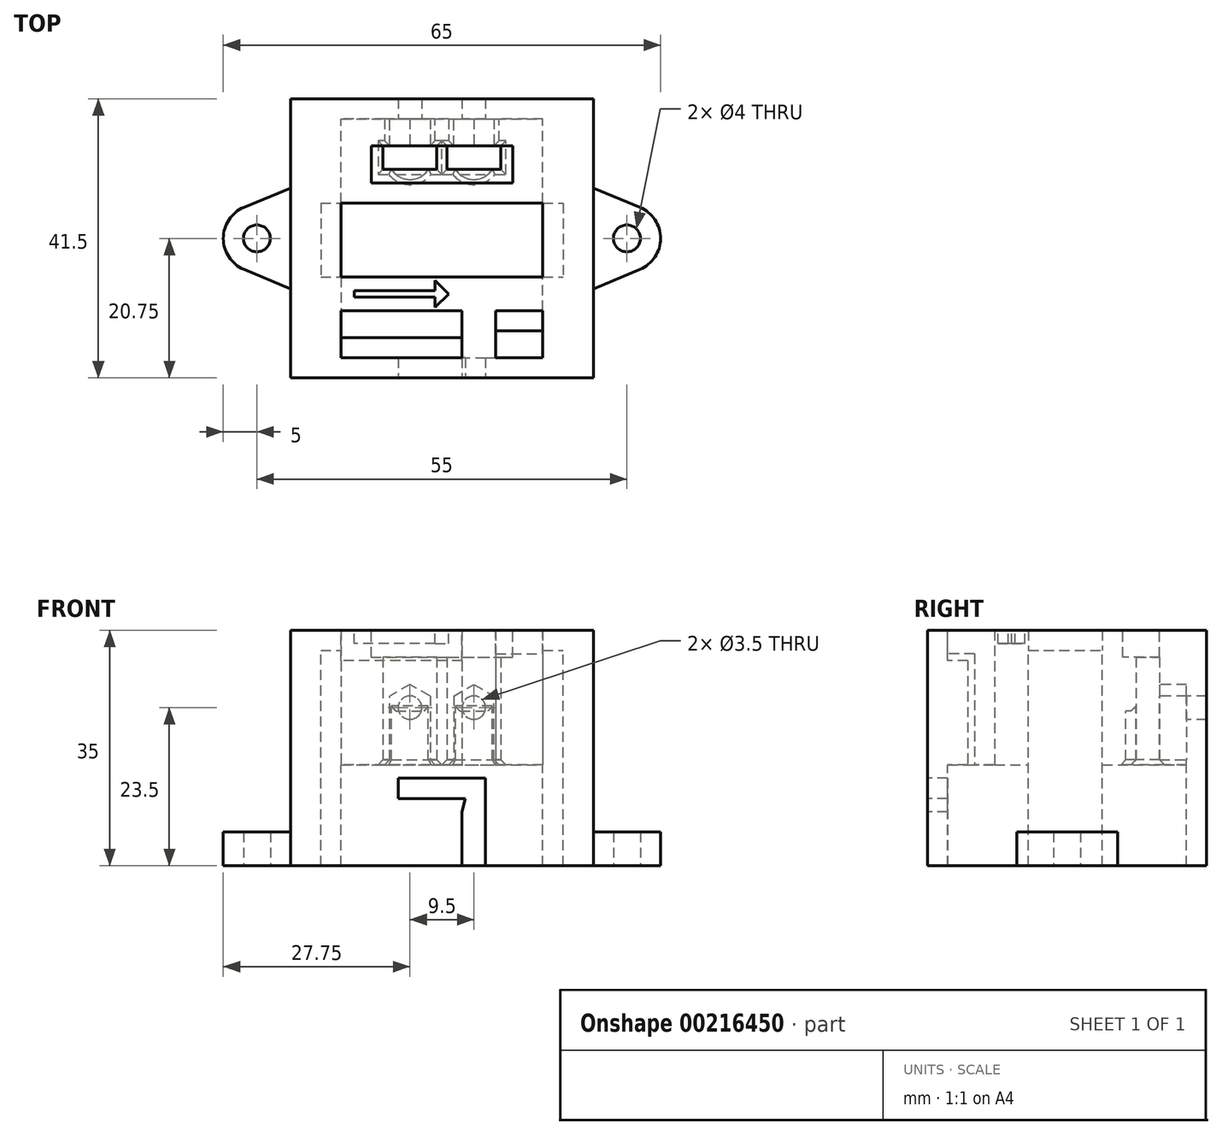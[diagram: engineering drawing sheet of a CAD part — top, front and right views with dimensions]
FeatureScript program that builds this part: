
annotation { "Feature Type Name" : "Feature", "Feature Type Description" : "" }
export const myFeature = defineFeature(function(context is Context, id is Id, definition is map)
    precondition{}
    {
        {
            var Q0;
            Q0=qCreatedBy(makeId("Top.planeOp"),FACE);
            var sketch = newSketch(context, id + "F0", { "sketchPlane" : qUnion([Q0])});
            skLineSegment(sketch, "E0.bottom", {"start": v(-22.5, 20.75) * mm, "end": v(22.5, 20.75) * mm});
            skLineSegment(sketch, "E0.top", {"start": v(-22.5, -20.75) * mm, "end": v(22.5, -20.75) * mm});
            skLineSegment(sketch, "E0.left", {"start": v(-22.5, 20.75) * mm, "end": v(-22.5, -20.75) * mm});
            skLineSegment(sketch, "E0.right", {"start": v(22.5, 20.75) * mm, "end": v(22.5, -20.75) * mm});
            skPoint(sketch, "E1", {"position": v(-22.5, 0) * mm});
            skPoint(sketch, "E2", {"position": v(0, 20.75) * mm});
            skLineSegment(sketch, "E3.bottom", {"start": v(-15, -5.75) * mm, "end": v(15, -5.75) * mm});
            skLineSegment(sketch, "E3.top", {"start": v(-15, 5.25) * mm, "end": v(15, 5.25) * mm});
            skLineSegment(sketch, "E3.left", {"start": v(-15, -5.75) * mm, "end": v(-15, 5.25) * mm});
            skLineSegment(sketch, "E3.right", {"start": v(15, -5.75) * mm, "end": v(15, 5.25) * mm});
            skPoint(sketch, "E4", {"position": v(0, 5.25) * mm});
            skLineSegment(sketch, "E5.bottom", {"start": v(-10.5, 13.75) * mm, "end": v(10.5, 13.75) * mm, "construction": true});
            skLineSegment(sketch, "E5.top", {"start": v(-10.5, 8.25) * mm, "end": v(10.5, 8.25) * mm, "construction": true});
            skLineSegment(sketch, "E5.left", {"start": v(-10.5, 13.75) * mm, "end": v(-10.5, 8.25) * mm, "construction": true});
            skLineSegment(sketch, "E5.right", {"start": v(10.5, 13.75) * mm, "end": v(10.5, 8.25) * mm, "construction": true});
            skPoint(sketch, "E6", {"position": v(0, 13.75) * mm});
            skLineSegment(sketch, "E7", {"start": v(0.75, 10.25) * mm, "end": v(0.75, 13.75) * mm});
            skLineSegment(sketch, "E8", {"start": v(0.75, 13.75) * mm, "end": v(8.75, 13.75) * mm});
            skLineSegment(sketch, "E9", {"start": v(8.75, 13.75) * mm, "end": v(8.75, 10.25) * mm});
            skLineSegment(sketch, "E10", {"start": v(0.75, 10.25) * mm, "end": v(8.75, 10.25) * mm});
            skLineSegment(sketch, "E11.MirrorCS", {"start": v(-0.75, 10.25) * mm, "end": v(-0.75, 13.75) * mm});
            skLineSegment(sketch, "E12.MirrorCS", {"start": v(-0.75, 13.75) * mm, "end": v(-8.75, 13.75) * mm});
            skLineSegment(sketch, "E13.MirrorCS", {"start": v(-8.75, 13.75) * mm, "end": v(-8.75, 10.25) * mm});
            skLineSegment(sketch, "E14", {"start": v(-0.75, 10.25) * mm, "end": v(-8.75, 10.25) * mm});
            skLineSegment(sketch, "E15", {"start": v(-15, -10.75) * mm, "end": v(3, -10.75) * mm});
            skLineSegment(sketch, "E16", {"start": v(-15, -10.75) * mm, "end": v(-15, -14.75) * mm});
            skLineSegment(sketch, "E17", {"start": v(3, -14.75) * mm, "end": v(-15, -14.75) * mm});
            skLineSegment(sketch, "E18", {"start": v(3, -14.75) * mm, "end": v(3, -10.75) * mm});
            skLineSegment(sketch, "E19", {"start": v(3, -14.75) * mm, "end": v(3, -17.75) * mm, "construction": true});
            skLineSegment(sketch, "E20", {"start": v(-15, -17.75) * mm, "end": v(3, -17.75) * mm, "construction": true});
            skLineSegment(sketch, "E21", {"start": v(-15, -17.75) * mm, "end": v(-15, -14.75) * mm, "construction": true});
            skLineSegment(sketch, "E22", {"start": v(8, -10.75) * mm, "end": v(8, -13.75) * mm});
            skLineSegment(sketch, "E23", {"start": v(8, -13.75) * mm, "end": v(15, -13.75) * mm});
            skLineSegment(sketch, "E24", {"start": v(15, -13.75) * mm, "end": v(15, -10.75) * mm});
            skLineSegment(sketch, "E25", {"start": v(15, -10.75) * mm, "end": v(8, -10.75) * mm});
            skLineSegment(sketch, "E26", {"start": v(8, -13.75) * mm, "end": v(8, -17.75) * mm, "construction": true});
            skLineSegment(sketch, "E27", {"start": v(8, -17.75) * mm, "end": v(15, -17.75) * mm, "construction": true});
            skLineSegment(sketch, "E28", {"start": v(15, -17.75) * mm, "end": v(15, -13.75) * mm, "construction": true});
            skLineSegment(sketch, "E29", {"start": v(-15, -20.75) * mm, "end": v(15, -20.75) * mm, "construction": true});
            skPoint(sketch, "E30", {"position": v(0, -20.75) * mm});
            skSolve(sketch);
        }
        {
            var Q0;
            Q0 = qSketchRegion(id + "F0", true);
            extrude(context, id + "F1", {"entities" : qUnion([Q0]), "depth" : 35 * mm});
        }
        {
            var Q0;
            Q0=makeQuery(id+"F1.opExtrude","CAP_FACE",FACE,{"disambiguationData":[OSD([sQuery(id+"F0.wireOp",EDGE,"E0.bottom"),sQuery(id+"F0.wireOp",EDGE,"E0.top"),sQuery(id+"F0.wireOp",EDGE,"E0.left"),sQuery(id+"F0.wireOp",EDGE,"E0.right"),sQuery(id+"F0.wireOp",EDGE,"E3.bottom"),sQuery(id+"F0.wireOp",EDGE,"E3.top"),sQuery(id+"F0.wireOp",EDGE,"E3.left"),sQuery(id+"F0.wireOp",EDGE,"E3.right"),sQuery(id+"F0.wireOp",EDGE,"E7"),sQuery(id+"F0.wireOp",EDGE,"E8"),sQuery(id+"F0.wireOp",EDGE,"E9"),sQuery(id+"F0.wireOp",EDGE,"E10"),sQuery(id+"F0.wireOp",EDGE,"E11.MirrorCS"),sQuery(id+"F0.wireOp",EDGE,"E12.MirrorCS"),sQuery(id+"F0.wireOp",EDGE,"E13.MirrorCS"),sQuery(id+"F0.wireOp",EDGE,"E14")])],"isStart":false});
            var sketch = newSketch(context, id + "F2", { "sketchPlane" : qUnion([Q0])});
            skLineSegment(sketch, "E31.bottom", {"start": v(-10.5, 13.75) * mm, "end": v(10.5, 13.75) * mm});
            skLineSegment(sketch, "E31.top", {"start": v(-10.5, 8.25) * mm, "end": v(10.5, 8.25) * mm});
            skLineSegment(sketch, "E31.left", {"start": v(-10.5, 13.75) * mm, "end": v(-10.5, 8.25) * mm});
            skLineSegment(sketch, "E31.right", {"start": v(10.5, 13.75) * mm, "end": v(10.5, 8.25) * mm});
            skSolve(sketch);
        }
        {
            var Q0;
            Q0 = qSketchRegion(id + "F2", true);
            extrude(context, id + "F3", {"entities" : qUnion([Q0]), "operationType" : NewBodyOperationType.REMOVE, "oppositeDirection" : true, "depth" : 4 * mm});
        }
        {
            var Q0;
            Q0=makeQuery(id+"F1.opExtrude","SWEPT_FACE",FACE,{"disambiguationData":[OSD([sQuery(id+"F0.wireOp",EDGE,"E8")])]});
            var sketch = newSketch(context, id + "F4", { "sketchPlane" : qUnion([Q0])});
            skCircle(sketch, "E32", {"center": v(4.75, 23.5) * mm, "radius": 1.75 * mm});
            skPoint(sketch, "E33", {"position": v(4.75, 31) * mm});
            skCircle(sketch, "E34.MirrorC", {"center": v(-4.75, 23.5) * mm, "radius": 1.75 * mm});
            skLineSegment(sketch, "E35", {"start": v(0.75, 31) * mm, "end": v(8.75, 31) * mm, "construction": true});
            skSolve(sketch);
        }
        {
            var Q0;
            Q0 = qSketchRegion(id + "F4", true);
            extrude(context, id + "F5", {"entities" : qUnion([Q0]), "operationType" : NewBodyOperationType.REMOVE, "oppositeDirection" : true, "depth" : 25 * mm});
        }
        {
            var Q0;
            Q0=makeQuery(id+"F1.opExtrude","SWEPT_FACE",FACE,{"disambiguationData":[OSD([sQuery(id+"F0.wireOp",EDGE,"E8")])]});
            var sketch = newSketch(context, id + "F6", { "sketchPlane" : qUnion([Q0])});
            skCircle(sketch, "E36.cCircle", {"center": v(4.75, 23.5) * mm, "radius": 3 * mm, "construction": true});
            skLineSegment(sketch, "E36.0", {"start": v(1.75, 25.23) * mm, "end": v(4.75, 26.96) * mm});
            skLineSegment(sketch, "E36.1", {"start": v(4.75, 26.96) * mm, "end": v(7.75, 25.23) * mm});
            skLineSegment(sketch, "E36.2", {"start": v(7.75, 25.23) * mm, "end": v(7.75, 21.77) * mm});
            skLineSegment(sketch, "E36.5", {"start": v(1.75, 21.77) * mm, "end": v(1.75, 25.23) * mm});
            skPoint(sketch, "E36.0.midPoint", {"position": v(3.25, 26.1) * mm});
            skLineSegment(sketch, "E37", {"start": v(1.75, 21.77) * mm, "end": v(1.75, -5.3) * mm});
            skLineSegment(sketch, "E38", {"start": v(1.75, -5.3) * mm, "end": v(7.75, -5.3) * mm});
            skLineSegment(sketch, "E39", {"start": v(7.75, -5.3) * mm, "end": v(7.75, 21.77) * mm});
            skLineSegment(sketch, "E40.MirrorCS", {"start": v(-1.75, 25.23) * mm, "end": v(-4.75, 26.96) * mm});
            skLineSegment(sketch, "E41.MirrorCS", {"start": v(-4.75, 26.96) * mm, "end": v(-7.75, 25.23) * mm});
            skLineSegment(sketch, "E42.MirrorCS", {"start": v(-7.75, 25.23) * mm, "end": v(-7.75, 21.77) * mm});
            skLineSegment(sketch, "E43.MirrorCS", {"start": v(-7.75, -5.3) * mm, "end": v(-7.75, 21.77) * mm});
            skLineSegment(sketch, "E44.MirrorCS", {"start": v(-1.75, -5.3) * mm, "end": v(-7.75, -5.3) * mm});
            skLineSegment(sketch, "E45.MirrorCS", {"start": v(-1.75, 21.77) * mm, "end": v(-1.75, -5.3) * mm});
            skLineSegment(sketch, "E46.MirrorCS", {"start": v(-1.75, 21.77) * mm, "end": v(-1.75, 25.23) * mm});
            skSolve(sketch);
        }
        {
            var Q0;
            Q0 = qSketchRegion(id + "F6", true);
            extrude(context, id + "F7", {"entities" : qUnion([Q0]), "operationType" : NewBodyOperationType.REMOVE, "oppositeDirection" : true, "depth" : 4 * mm});
        }
        {
            var Q0;
            Q0=makeQuery(id+"F3.boolean.opBoolean","COPY",FACE,{"derivedFrom":makeQuery(id+"F3.opExtrude","CAP_FACE",FACE,{"disambiguationData":[OSD([sQuery(id+"F2.wireOp",EDGE,"E31.bottom"),sQuery(id+"F2.wireOp",EDGE,"E31.top"),sQuery(id+"F2.wireOp",EDGE,"E31.left"),sQuery(id+"F2.wireOp",EDGE,"E31.right")])],"isStart":false})});
            var sketch = newSketch(context, id + "F8", { "sketchPlane" : qUnion([Q0])});
            skPoint(sketch, "E47", {"position": v(4.75, 12) * mm});
            skPoint(sketch, "E48", {"position": v(8.75, 12) * mm});
            skCircle(sketch, "E49", {"center": v(4.75, 12) * mm, "radius": 3.25 * mm});
            skCircle(sketch, "E50.MirrorC", {"center": v(-4.75, 12) * mm, "radius": 3.25 * mm});
            skLineSegment(sketch, "E51", {"start": v(-8.75, 12) * mm, "end": v(-0.75, 12) * mm, "construction": true});
            skSolve(sketch);
        }
        {
            var Q0;
            Q0 = qSketchRegion(id + "F8", true);
            extrude(context, id + "F9", {"entities" : qUnion([Q0]), "operationType" : NewBodyOperationType.REMOVE, "oppositeDirection" : true, "depth" : 25 * mm, "hasSecondDirection" : true, "secondDirectionOppositeDirection" : true, "secondDirectionDepth" : 8 * mm});
        }
        {
            var Q0;
            Q0=makeQuery(id+"F1.opExtrude","CAP_FACE",FACE,{"disambiguationData":[OSD([sQuery(id+"F0.wireOp",EDGE,"E0.bottom"),sQuery(id+"F0.wireOp",EDGE,"E0.top"),sQuery(id+"F0.wireOp",EDGE,"E0.left"),sQuery(id+"F0.wireOp",EDGE,"E0.right"),sQuery(id+"F0.wireOp",EDGE,"E3.bottom"),sQuery(id+"F0.wireOp",EDGE,"E3.top"),sQuery(id+"F0.wireOp",EDGE,"E3.left"),sQuery(id+"F0.wireOp",EDGE,"E3.right"),sQuery(id+"F0.wireOp",EDGE,"E7"),sQuery(id+"F0.wireOp",EDGE,"E8"),sQuery(id+"F0.wireOp",EDGE,"E9"),sQuery(id+"F0.wireOp",EDGE,"E10"),sQuery(id+"F0.wireOp",EDGE,"E11.MirrorCS"),sQuery(id+"F0.wireOp",EDGE,"E12.MirrorCS"),sQuery(id+"F0.wireOp",EDGE,"E13.MirrorCS"),sQuery(id+"F0.wireOp",EDGE,"E14")])],"isStart":false});
            var sketch = newSketch(context, id + "F10", { "sketchPlane" : qUnion([Q0])});
            skLineSegment(sketch, "E52.bottom", {"start": v(-18, 5.25) * mm, "end": v(18, 5.25) * mm});
            skLineSegment(sketch, "E52.top", {"start": v(-18, -5.75) * mm, "end": v(18, -5.75) * mm});
            skLineSegment(sketch, "E52.left", {"start": v(-18, 5.25) * mm, "end": v(-18, -5.75) * mm});
            skLineSegment(sketch, "E52.right", {"start": v(18, 5.25) * mm, "end": v(18, -5.75) * mm});
            skPoint(sketch, "E53", {"position": v(0, 5.25) * mm});
            skSolve(sketch);
        }
        {
            var Q0;
            Q0 = qSketchRegion(id + "F10", true);
            extrude(context, id + "F11", {"entities" : qUnion([Q0]), "operationType" : NewBodyOperationType.REMOVE, "endBound" : BoundingType.THROUGH_ALL, "oppositeDirection" : true, "depth" : 25 * mm, "hasSecondDirection" : true, "secondDirectionOppositeDirection" : true, "secondDirectionDepth" : 3 * mm});
        }
        {
            var Q0;
            Q0=makeQuery(id+"F1.opExtrude","CAP_FACE",FACE,{"disambiguationData":[OSD([sQuery(id+"F0.wireOp",EDGE,"E0.bottom"),sQuery(id+"F0.wireOp",EDGE,"E0.top"),sQuery(id+"F0.wireOp",EDGE,"E0.left"),sQuery(id+"F0.wireOp",EDGE,"E0.right"),sQuery(id+"F0.wireOp",EDGE,"E3.bottom"),sQuery(id+"F0.wireOp",EDGE,"E3.top"),sQuery(id+"F0.wireOp",EDGE,"E3.left"),sQuery(id+"F0.wireOp",EDGE,"E3.right"),sQuery(id+"F0.wireOp",EDGE,"E7"),sQuery(id+"F0.wireOp",EDGE,"E8"),sQuery(id+"F0.wireOp",EDGE,"E9"),sQuery(id+"F0.wireOp",EDGE,"E10"),sQuery(id+"F0.wireOp",EDGE,"E11.MirrorCS"),sQuery(id+"F0.wireOp",EDGE,"E12.MirrorCS"),sQuery(id+"F0.wireOp",EDGE,"E13.MirrorCS"),sQuery(id+"F0.wireOp",EDGE,"E14"),sQuery(id+"F0.wireOp",EDGE,"E15"),sQuery(id+"F0.wireOp",EDGE,"E16"),sQuery(id+"F0.wireOp",EDGE,"E17"),sQuery(id+"F0.wireOp",EDGE,"E18")])],"isStart":false});
            var sketch = newSketch(context, id + "F12", { "sketchPlane" : qUnion([Q0])});
            skLineSegment(sketch, "E54.bottom", {"start": v(-15, -10.75) * mm, "end": v(3, -10.75) * mm});
            skLineSegment(sketch, "E54.top", {"start": v(-15, -17.75) * mm, "end": v(3, -17.75) * mm});
            skLineSegment(sketch, "E54.left", {"start": v(-15, -10.75) * mm, "end": v(-15, -17.75) * mm});
            skLineSegment(sketch, "E54.right", {"start": v(3, -10.75) * mm, "end": v(3, -17.75) * mm});
            skSolve(sketch);
        }
        {
            var Q0;
            Q0 = qSketchRegion(id + "F12", true);
            extrude(context, id + "F13", {"entities" : qUnion([Q0]), "operationType" : NewBodyOperationType.REMOVE, "oppositeDirection" : true, "depth" : 4.5 * mm});
        }
        {
            var Q0;
            Q0=makeQuery(id+"F1.opExtrude","CAP_FACE",FACE,{"disambiguationData":[OSD([sQuery(id+"F0.wireOp",EDGE,"E0.bottom"),sQuery(id+"F0.wireOp",EDGE,"E0.top"),sQuery(id+"F0.wireOp",EDGE,"E0.left"),sQuery(id+"F0.wireOp",EDGE,"E0.right"),sQuery(id+"F0.wireOp",EDGE,"E3.bottom"),sQuery(id+"F0.wireOp",EDGE,"E3.top"),sQuery(id+"F0.wireOp",EDGE,"E3.left"),sQuery(id+"F0.wireOp",EDGE,"E3.right"),sQuery(id+"F0.wireOp",EDGE,"E7"),sQuery(id+"F0.wireOp",EDGE,"E8"),sQuery(id+"F0.wireOp",EDGE,"E9"),sQuery(id+"F0.wireOp",EDGE,"E10"),sQuery(id+"F0.wireOp",EDGE,"E11.MirrorCS"),sQuery(id+"F0.wireOp",EDGE,"E12.MirrorCS"),sQuery(id+"F0.wireOp",EDGE,"E13.MirrorCS"),sQuery(id+"F0.wireOp",EDGE,"E14"),sQuery(id+"F0.wireOp",EDGE,"E15"),sQuery(id+"F0.wireOp",EDGE,"E16"),sQuery(id+"F0.wireOp",EDGE,"E17"),sQuery(id+"F0.wireOp",EDGE,"E18"),sQuery(id+"F0.wireOp",EDGE,"E22"),sQuery(id+"F0.wireOp",EDGE,"E23"),sQuery(id+"F0.wireOp",EDGE,"E24"),sQuery(id+"F0.wireOp",EDGE,"E25")])],"isStart":false});
            var sketch = newSketch(context, id + "F14", { "sketchPlane" : qUnion([Q0])});
            skLineSegment(sketch, "E55.bottom", {"start": v(8, -13.75) * mm, "end": v(15, -13.75) * mm});
            skLineSegment(sketch, "E55.top", {"start": v(8, -17.75) * mm, "end": v(15, -17.75) * mm});
            skLineSegment(sketch, "E55.left", {"start": v(8, -13.75) * mm, "end": v(8, -17.75) * mm});
            skLineSegment(sketch, "E55.right", {"start": v(15, -13.75) * mm, "end": v(15, -17.75) * mm});
            skSolve(sketch);
        }
        {
            var Q0;
            Q0 = qSketchRegion(id + "F14", true);
            extrude(context, id + "F15", {"entities" : qUnion([Q0]), "operationType" : NewBodyOperationType.REMOVE, "oppositeDirection" : true, "depth" : 3.5 * mm});
        }
        {
            var Q0;
            Q0=makeQuery(id+"F1.opExtrude","CAP_FACE",FACE,{"disambiguationData":[OSD([sQuery(id+"F0.wireOp",EDGE,"E0.bottom"),sQuery(id+"F0.wireOp",EDGE,"E0.top"),sQuery(id+"F0.wireOp",EDGE,"E0.left"),sQuery(id+"F0.wireOp",EDGE,"E0.right"),sQuery(id+"F0.wireOp",EDGE,"E3.bottom"),sQuery(id+"F0.wireOp",EDGE,"E3.top"),sQuery(id+"F0.wireOp",EDGE,"E3.left"),sQuery(id+"F0.wireOp",EDGE,"E3.right"),sQuery(id+"F0.wireOp",EDGE,"E7"),sQuery(id+"F0.wireOp",EDGE,"E8"),sQuery(id+"F0.wireOp",EDGE,"E9"),sQuery(id+"F0.wireOp",EDGE,"E10"),sQuery(id+"F0.wireOp",EDGE,"E11.MirrorCS"),sQuery(id+"F0.wireOp",EDGE,"E12.MirrorCS"),sQuery(id+"F0.wireOp",EDGE,"E13.MirrorCS"),sQuery(id+"F0.wireOp",EDGE,"E14")])],"isStart":false});
            var sketch = newSketch(context, id + "F16", { "sketchPlane" : qUnion([Q0])});
            skLineSegment(sketch, "E56.bottom", {"start": v(15, 5.25) * mm, "end": v(-15, 5.25) * mm});
            skLineSegment(sketch, "E56.top", {"start": v(15, 17.75) * mm, "end": v(-15, 17.75) * mm});
            skLineSegment(sketch, "E56.left", {"start": v(15, 5.25) * mm, "end": v(15, 17.75) * mm});
            skLineSegment(sketch, "E56.right", {"start": v(-15, 5.25) * mm, "end": v(-15, 17.75) * mm});
            skLineSegment(sketch, "E57.top", {"start": v(-15, -5.75) * mm, "end": v(15, -5.75) * mm});
            skLineSegment(sketch, "E57.left", {"start": v(-15, -17.75) * mm, "end": v(-15, -5.75) * mm});
            skLineSegment(sketch, "E57.right", {"start": v(15, -17.75) * mm, "end": v(15, -5.75) * mm});
            skLineSegment(sketch, "E58", {"start": v(-15, -17.75) * mm, "end": v(15, -17.75) * mm});
            skSolve(sketch);
        }
        {
            var Q0;
            Q0 = qSketchRegion(id + "F16", true);
            extrude(context, id + "F17", {"entities" : qUnion([Q0]), "operationType" : NewBodyOperationType.REMOVE, "endBound" : BoundingType.THROUGH_ALL, "oppositeDirection" : true, "depth" : 25 * mm, "hasSecondDirection" : true, "secondDirectionOppositeDirection" : true, "secondDirectionDepth" : 20 * mm});
        }
        {
            var Q0;
            Q0=makeQuery(id+"F1.opExtrude","CAP_FACE",FACE,{"disambiguationData":[OSD([sQuery(id+"F0.wireOp",EDGE,"E0.bottom"),sQuery(id+"F0.wireOp",EDGE,"E0.top"),sQuery(id+"F0.wireOp",EDGE,"E0.left"),sQuery(id+"F0.wireOp",EDGE,"E0.right"),sQuery(id+"F0.wireOp",EDGE,"E3.bottom"),sQuery(id+"F0.wireOp",EDGE,"E3.top"),sQuery(id+"F0.wireOp",EDGE,"E3.left"),sQuery(id+"F0.wireOp",EDGE,"E3.right"),sQuery(id+"F0.wireOp",EDGE,"E7"),sQuery(id+"F0.wireOp",EDGE,"E8"),sQuery(id+"F0.wireOp",EDGE,"E9"),sQuery(id+"F0.wireOp",EDGE,"E10"),sQuery(id+"F0.wireOp",EDGE,"E11.MirrorCS"),sQuery(id+"F0.wireOp",EDGE,"E12.MirrorCS"),sQuery(id+"F0.wireOp",EDGE,"E13.MirrorCS"),sQuery(id+"F0.wireOp",EDGE,"E14"),sQuery(id+"F0.wireOp",EDGE,"E15"),sQuery(id+"F0.wireOp",EDGE,"E16"),sQuery(id+"F0.wireOp",EDGE,"E17"),sQuery(id+"F0.wireOp",EDGE,"E18")])],"isStart":false});
            var sketch = newSketch(context, id + "F18", { "sketchPlane" : qUnion([Q0])});
            skLineSegment(sketch, "E59", {"start": v(-13, -7.75) * mm, "end": v(-13, -8.75) * mm});
            skLineSegment(sketch, "E60", {"start": v(-13, -8.75) * mm, "end": v(-1, -8.75) * mm});
            skLineSegment(sketch, "E61", {"start": v(-1, -8.75) * mm, "end": v(-1, -10.25) * mm});
            skLineSegment(sketch, "E62", {"start": v(-1, -10.25) * mm, "end": v(1, -8.25) * mm});
            skLineSegment(sketch, "E63", {"start": v(1, -8.25) * mm, "end": v(-1, -6.25) * mm});
            skLineSegment(sketch, "E64", {"start": v(-1, -6.25) * mm, "end": v(-1, -7.75) * mm});
            skLineSegment(sketch, "E65", {"start": v(-1, -7.75) * mm, "end": v(-13, -7.75) * mm});
            skPoint(sketch, "E66", {"position": v(-13, -8.25) * mm});
            skLineSegment(sketch, "E67", {"start": v(-13, -8.25) * mm, "end": v(1, -8.25) * mm, "construction": true});
            skPoint(sketch, "E68", {"position": v(-6, -8.25) * mm});
            skPoint(sketch, "E69", {"position": v(-6, -10.75) * mm});
            skLineSegment(sketch, "E70", {"start": v(-13, -5.75) * mm, "end": v(-13, -10.75) * mm, "construction": true});
            skSolve(sketch);
        }
        {
            var Q0;
            Q0 = qSketchRegion(id + "F18", true);
            extrude(context, id + "F19", {"entities" : qUnion([Q0]), "operationType" : NewBodyOperationType.REMOVE, "oppositeDirection" : true, "depth" : 2 * mm});
        }
        {
            var Q0;
            Q0=qCreatedBy(makeId("Top.planeOp"),FACE);
            var sketch = newSketch(context, id + "F20", { "sketchPlane" : qUnion([Q0])});
            skCircle(sketch, "E71", {"center": v(-27.5, 0) * mm, "radius": 2 * mm});
            skCircle(sketch, "E72.MirrorC", {"center": v(27.5, 0) * mm, "radius": 2 * mm});
            skArc(sketch, "E73", {"start": v(29.42, -4.62) * mm, "mid": v(32.5, 0) * mm, "end": v(29.42, 4.62) * mm});
            skLineSegment(sketch, "E74", {"start": v(22.5, -7.5) * mm, "end": v(22.5, 7.5) * mm});
            skLineSegment(sketch, "E75", {"start": v(22.5, 7.5) * mm, "end": v(29.42, 4.62) * mm});
            skLineSegment(sketch, "E76.MirrorCS", {"start": v(-22.5, -7.5) * mm, "end": v(-22.5, 7.5) * mm});
            skLineSegment(sketch, "E77.MirrorCS", {"start": v(-29.42, -4.62) * mm, "end": v(-22.5, -7.5) * mm});
            skArc(sketch, "E78.MirrorCS", {"start": v(-29.42, -4.62) * mm, "mid": v(-32.5, 0) * mm, "end": v(-29.42, 4.62) * mm});
            skLineSegment(sketch, "E79.MirrorCS", {"start": v(-22.5, 7.5) * mm, "end": v(-29.42, 4.62) * mm});
            skLineSegment(sketch, "E80.MirrorCS", {"start": v(22.5, -7.5) * mm, "end": v(29.42, -4.62) * mm});
            skSolve(sketch);
        }
        {
            var Q0;
            Q0 = qSketchRegion(id + "F20", true);
            extrude(context, id + "F21", {"entities" : qUnion([Q0]), "operationType" : NewBodyOperationType.ADD, "depth" : 5 * mm});
        }
        {
            var Q0;
            Q0=makeQuery(id+"F1.opExtrude","SWEPT_FACE",FACE,{"disambiguationData":[OSD([sQuery(id+"F0.wireOp",EDGE,"E0.top")])]});
            var sketch = newSketch(context, id + "F22", { "sketchPlane" : qUnion([Q0])});
            skLineSegment(sketch, "E81", {"start": v(3, 0) * mm, "end": v(3, 8) * mm});
            skLineSegment(sketch, "E82", {"start": v(6.5, 13) * mm, "end": v(6.5, 0) * mm});
            skLineSegment(sketch, "E83", {"start": v(3, 8) * mm, "end": v(3.5, 10) * mm});
            skLineSegment(sketch, "E84", {"start": v(3.5, 10) * mm, "end": v(-6.5, 10) * mm});
            skLineSegment(sketch, "E85", {"start": v(-6.5, 10) * mm, "end": v(-6.5, 13) * mm});
            skLineSegment(sketch, "E86", {"start": v(-6.5, 13) * mm, "end": v(6.5, 13) * mm});
            skPoint(sketch, "E87", {"position": v(0, 13) * mm});
            skLineSegment(sketch, "E88", {"start": v(3, 0) * mm, "end": v(6.5, 0) * mm});
            skSolve(sketch);
        }
        {
            var Q0;
            Q0 = qSketchRegion(id + "F22", true);
            extrude(context, id + "F23", {"entities" : qUnion([Q0]), "operationType" : NewBodyOperationType.REMOVE, "oppositeDirection" : true, "depth" : 10 * mm});
        }
        {
            var Q0;
            Q0=makeQuery(id+"F17.boolean.opBoolean","INTERSECT",EDGE,{"derivedFrom":[makeQuery(id+"F7.boolean.opBoolean","COPY",FACE,{"derivedFrom":makeQuery(id+"F7.opExtrude","SWEPT_FACE",FACE,{"disambiguationData":[OSD([sQuery(id+"F6.wireOp",EDGE,"E42.MirrorCS"),sQuery(id+"F6.wireOp",EDGE,"E43.MirrorCS")])]})}),makeQuery(id+"F17.opExtrude","CAP_FACE",FACE,{"disambiguationData":[OSD([sQuery(id+"F16.wireOp",EDGE,"E56.bottom"),sQuery(id+"F16.wireOp",EDGE,"E56.top"),sQuery(id+"F16.wireOp",EDGE,"E56.left"),sQuery(id+"F16.wireOp",EDGE,"E56.right")])],"isStart":true})]});
            var Q1;
            Q1=makeQuery(id+"F17.boolean.opBoolean","INTERSECT",EDGE,{"derivedFrom":[makeQuery(id+"F9.boolean.opBoolean","COPY",FACE,{"derivedFrom":makeQuery(id+"F9.opExtrude","SWEPT_FACE",FACE,{"disambiguationData":[OSD([sQuery(id+"F8.wireOp",EDGE,"E50.MirrorC")])]})}),makeQuery(id+"F17.opExtrude","CAP_FACE",FACE,{"disambiguationData":[OSD([sQuery(id+"F16.wireOp",EDGE,"E56.bottom"),sQuery(id+"F16.wireOp",EDGE,"E56.top"),sQuery(id+"F16.wireOp",EDGE,"E56.left"),sQuery(id+"F16.wireOp",EDGE,"E56.right")])],"isStart":true})]});
            var Q2;
            Q2=makeQuery(id+"F17.boolean.opBoolean","INTERSECT",EDGE,{"disambiguationData":[OD(3.0)],"derivedFrom":[makeQuery(id+"F3.boolean.opBoolean","MERGE",FACE,{"derivedFrom":[makeQuery(id+"F1.opExtrude","SWEPT_FACE",FACE,{"disambiguationData":[OSD([sQuery(id+"F0.wireOp",EDGE,"E10")])]}),makeQuery(id+"F1.opExtrude","SWEPT_FACE",FACE,{"disambiguationData":[OSD([sQuery(id+"F0.wireOp",EDGE,"E14")])]}),makeQuery(id+"F3.opExtrude","SWEPT_FACE",FACE,{"disambiguationData":[OSD([sQuery(id+"F2.wireOp",EDGE,"E31.top")])]})]}),makeQuery(id+"F17.opExtrude","CAP_FACE",FACE,{"disambiguationData":[OSD([sQuery(id+"F16.wireOp",EDGE,"E56.bottom"),sQuery(id+"F16.wireOp",EDGE,"E56.top"),sQuery(id+"F16.wireOp",EDGE,"E56.left"),sQuery(id+"F16.wireOp",EDGE,"E56.right")])],"isStart":true})]});
            var Q3;
            Q3=makeQuery(id+"F17.boolean.opBoolean","INTERSECT",EDGE,{"derivedFrom":[makeQuery(id+"F1.opExtrude","SWEPT_FACE",FACE,{"disambiguationData":[OSD([sQuery(id+"F0.wireOp",EDGE,"E13.MirrorCS")])]}),makeQuery(id+"F17.opExtrude","CAP_FACE",FACE,{"disambiguationData":[OSD([sQuery(id+"F16.wireOp",EDGE,"E56.bottom"),sQuery(id+"F16.wireOp",EDGE,"E56.top"),sQuery(id+"F16.wireOp",EDGE,"E56.left"),sQuery(id+"F16.wireOp",EDGE,"E56.right")])],"isStart":true})]});
            var Q4;
            Q4=makeQuery(id+"F17.boolean.opBoolean","INTERSECT",EDGE,{"disambiguationData":[OD(1.0)],"derivedFrom":[makeQuery(id+"F1.opExtrude","SWEPT_FACE",FACE,{"disambiguationData":[OSD([sQuery(id+"F0.wireOp",EDGE,"E12.MirrorCS")])]}),makeQuery(id+"F17.opExtrude","CAP_FACE",FACE,{"disambiguationData":[OSD([sQuery(id+"F16.wireOp",EDGE,"E56.bottom"),sQuery(id+"F16.wireOp",EDGE,"E56.top"),sQuery(id+"F16.wireOp",EDGE,"E56.left"),sQuery(id+"F16.wireOp",EDGE,"E56.right")])],"isStart":true})]});
            var Q5;
            Q5=makeQuery(id+"F17.boolean.opBoolean","INTERSECT",EDGE,{"derivedFrom":[makeQuery(id+"F7.boolean.opBoolean","COPY",FACE,{"derivedFrom":makeQuery(id+"F7.opExtrude","SWEPT_FACE",FACE,{"disambiguationData":[OSD([sQuery(id+"F6.wireOp",EDGE,"E45.MirrorCS"),sQuery(id+"F6.wireOp",EDGE,"E46.MirrorCS")])]})}),makeQuery(id+"F17.opExtrude","CAP_FACE",FACE,{"disambiguationData":[OSD([sQuery(id+"F16.wireOp",EDGE,"E56.bottom"),sQuery(id+"F16.wireOp",EDGE,"E56.top"),sQuery(id+"F16.wireOp",EDGE,"E56.left"),sQuery(id+"F16.wireOp",EDGE,"E56.right")])],"isStart":true})]});
            var Q6;
            Q6=makeQuery(id+"F17.boolean.opBoolean","INTERSECT",EDGE,{"disambiguationData":[OD(0.0)],"derivedFrom":[makeQuery(id+"F1.opExtrude","SWEPT_FACE",FACE,{"disambiguationData":[OSD([sQuery(id+"F0.wireOp",EDGE,"E12.MirrorCS")])]}),makeQuery(id+"F17.opExtrude","CAP_FACE",FACE,{"disambiguationData":[OSD([sQuery(id+"F16.wireOp",EDGE,"E56.bottom"),sQuery(id+"F16.wireOp",EDGE,"E56.top"),sQuery(id+"F16.wireOp",EDGE,"E56.left"),sQuery(id+"F16.wireOp",EDGE,"E56.right")])],"isStart":true})]});
            var Q7;
            Q7=makeQuery(id+"F17.boolean.opBoolean","INTERSECT",EDGE,{"disambiguationData":[OD(2.0)],"derivedFrom":[makeQuery(id+"F3.boolean.opBoolean","MERGE",FACE,{"derivedFrom":[makeQuery(id+"F1.opExtrude","SWEPT_FACE",FACE,{"disambiguationData":[OSD([sQuery(id+"F0.wireOp",EDGE,"E10")])]}),makeQuery(id+"F1.opExtrude","SWEPT_FACE",FACE,{"disambiguationData":[OSD([sQuery(id+"F0.wireOp",EDGE,"E14")])]}),makeQuery(id+"F3.opExtrude","SWEPT_FACE",FACE,{"disambiguationData":[OSD([sQuery(id+"F2.wireOp",EDGE,"E31.top")])]})]}),makeQuery(id+"F17.opExtrude","CAP_FACE",FACE,{"disambiguationData":[OSD([sQuery(id+"F16.wireOp",EDGE,"E56.bottom"),sQuery(id+"F16.wireOp",EDGE,"E56.top"),sQuery(id+"F16.wireOp",EDGE,"E56.left"),sQuery(id+"F16.wireOp",EDGE,"E56.right")])],"isStart":true})]});
            var Q8;
            Q8=makeQuery(id+"F17.boolean.opBoolean","INTERSECT",EDGE,{"derivedFrom":[makeQuery(id+"F7.boolean.opBoolean","COPY",FACE,{"derivedFrom":makeQuery(id+"F7.opExtrude","SWEPT_FACE",FACE,{"disambiguationData":[OSD([sQuery(id+"F6.wireOp",EDGE,"E36.5"),sQuery(id+"F6.wireOp",EDGE,"E37")])]})}),makeQuery(id+"F17.opExtrude","CAP_FACE",FACE,{"disambiguationData":[OSD([sQuery(id+"F16.wireOp",EDGE,"E56.bottom"),sQuery(id+"F16.wireOp",EDGE,"E56.top"),sQuery(id+"F16.wireOp",EDGE,"E56.left"),sQuery(id+"F16.wireOp",EDGE,"E56.right")])],"isStart":true})]});
            var Q9;
            Q9=makeQuery(id+"F17.boolean.opBoolean","INTERSECT",EDGE,{"disambiguationData":[OD(0.0)],"derivedFrom":[makeQuery(id+"F1.opExtrude","SWEPT_FACE",FACE,{"disambiguationData":[OSD([sQuery(id+"F0.wireOp",EDGE,"E8")])]}),makeQuery(id+"F17.opExtrude","CAP_FACE",FACE,{"disambiguationData":[OSD([sQuery(id+"F16.wireOp",EDGE,"E56.bottom"),sQuery(id+"F16.wireOp",EDGE,"E56.top"),sQuery(id+"F16.wireOp",EDGE,"E56.left"),sQuery(id+"F16.wireOp",EDGE,"E56.right")])],"isStart":true})]});
            var Q10;
            Q10=makeQuery(id+"F17.boolean.opBoolean","INTERSECT",EDGE,{"disambiguationData":[OD(0.0)],"derivedFrom":[makeQuery(id+"F3.boolean.opBoolean","MERGE",FACE,{"derivedFrom":[makeQuery(id+"F1.opExtrude","SWEPT_FACE",FACE,{"disambiguationData":[OSD([sQuery(id+"F0.wireOp",EDGE,"E10")])]}),makeQuery(id+"F1.opExtrude","SWEPT_FACE",FACE,{"disambiguationData":[OSD([sQuery(id+"F0.wireOp",EDGE,"E14")])]}),makeQuery(id+"F3.opExtrude","SWEPT_FACE",FACE,{"disambiguationData":[OSD([sQuery(id+"F2.wireOp",EDGE,"E31.top")])]})]}),makeQuery(id+"F17.opExtrude","CAP_FACE",FACE,{"disambiguationData":[OSD([sQuery(id+"F16.wireOp",EDGE,"E56.bottom"),sQuery(id+"F16.wireOp",EDGE,"E56.top"),sQuery(id+"F16.wireOp",EDGE,"E56.left"),sQuery(id+"F16.wireOp",EDGE,"E56.right")])],"isStart":true})]});
            var Q11;
            Q11=makeQuery(id+"F17.boolean.opBoolean","INTERSECT",EDGE,{"derivedFrom":[makeQuery(id+"F9.boolean.opBoolean","COPY",FACE,{"derivedFrom":makeQuery(id+"F9.opExtrude","SWEPT_FACE",FACE,{"disambiguationData":[OSD([sQuery(id+"F8.wireOp",EDGE,"E49")])]})}),makeQuery(id+"F17.opExtrude","CAP_FACE",FACE,{"disambiguationData":[OSD([sQuery(id+"F16.wireOp",EDGE,"E56.bottom"),sQuery(id+"F16.wireOp",EDGE,"E56.top"),sQuery(id+"F16.wireOp",EDGE,"E56.left"),sQuery(id+"F16.wireOp",EDGE,"E56.right")])],"isStart":true})]});
            var Q12;
            Q12=makeQuery(id+"F17.boolean.opBoolean","INTERSECT",EDGE,{"disambiguationData":[OD(1.0)],"derivedFrom":[makeQuery(id+"F3.boolean.opBoolean","MERGE",FACE,{"derivedFrom":[makeQuery(id+"F1.opExtrude","SWEPT_FACE",FACE,{"disambiguationData":[OSD([sQuery(id+"F0.wireOp",EDGE,"E10")])]}),makeQuery(id+"F1.opExtrude","SWEPT_FACE",FACE,{"disambiguationData":[OSD([sQuery(id+"F0.wireOp",EDGE,"E14")])]}),makeQuery(id+"F3.opExtrude","SWEPT_FACE",FACE,{"disambiguationData":[OSD([sQuery(id+"F2.wireOp",EDGE,"E31.top")])]})]}),makeQuery(id+"F17.opExtrude","CAP_FACE",FACE,{"disambiguationData":[OSD([sQuery(id+"F16.wireOp",EDGE,"E56.bottom"),sQuery(id+"F16.wireOp",EDGE,"E56.top"),sQuery(id+"F16.wireOp",EDGE,"E56.left"),sQuery(id+"F16.wireOp",EDGE,"E56.right")])],"isStart":true})]});
            var Q13;
            Q13=makeQuery(id+"F17.boolean.opBoolean","INTERSECT",EDGE,{"derivedFrom":[makeQuery(id+"F1.opExtrude","SWEPT_FACE",FACE,{"disambiguationData":[OSD([sQuery(id+"F0.wireOp",EDGE,"E9")])]}),makeQuery(id+"F17.opExtrude","CAP_FACE",FACE,{"disambiguationData":[OSD([sQuery(id+"F16.wireOp",EDGE,"E56.bottom"),sQuery(id+"F16.wireOp",EDGE,"E56.top"),sQuery(id+"F16.wireOp",EDGE,"E56.left"),sQuery(id+"F16.wireOp",EDGE,"E56.right")])],"isStart":true})]});
            var Q14;
            Q14=makeQuery(id+"F17.boolean.opBoolean","INTERSECT",EDGE,{"disambiguationData":[OD(1.0)],"derivedFrom":[makeQuery(id+"F1.opExtrude","SWEPT_FACE",FACE,{"disambiguationData":[OSD([sQuery(id+"F0.wireOp",EDGE,"E8")])]}),makeQuery(id+"F17.opExtrude","CAP_FACE",FACE,{"disambiguationData":[OSD([sQuery(id+"F16.wireOp",EDGE,"E56.bottom"),sQuery(id+"F16.wireOp",EDGE,"E56.top"),sQuery(id+"F16.wireOp",EDGE,"E56.left"),sQuery(id+"F16.wireOp",EDGE,"E56.right")])],"isStart":true})]});
            var Q15;
            Q15=makeQuery(id+"F17.boolean.opBoolean","INTERSECT",EDGE,{"derivedFrom":[makeQuery(id+"F7.boolean.opBoolean","COPY",FACE,{"derivedFrom":makeQuery(id+"F7.opExtrude","SWEPT_FACE",FACE,{"disambiguationData":[OSD([sQuery(id+"F6.wireOp",EDGE,"E36.2"),sQuery(id+"F6.wireOp",EDGE,"E39")])]})}),makeQuery(id+"F17.opExtrude","CAP_FACE",FACE,{"disambiguationData":[OSD([sQuery(id+"F16.wireOp",EDGE,"E56.bottom"),sQuery(id+"F16.wireOp",EDGE,"E56.top"),sQuery(id+"F16.wireOp",EDGE,"E56.left"),sQuery(id+"F16.wireOp",EDGE,"E56.right")])],"isStart":true})]});
            var Q16;
            Q16=makeQuery(id+"F17.boolean.opBoolean","INTERSECT",EDGE,{"derivedFrom":[makeQuery(id+"F1.opExtrude","SWEPT_FACE",FACE,{"disambiguationData":[OSD([sQuery(id+"F0.wireOp",EDGE,"E11.MirrorCS")])]}),makeQuery(id+"F17.opExtrude","CAP_FACE",FACE,{"disambiguationData":[OSD([sQuery(id+"F16.wireOp",EDGE,"E56.bottom"),sQuery(id+"F16.wireOp",EDGE,"E56.top"),sQuery(id+"F16.wireOp",EDGE,"E56.left"),sQuery(id+"F16.wireOp",EDGE,"E56.right")])],"isStart":true})]});
            var Q17;
            Q17=makeQuery(id+"F17.boolean.opBoolean","INTERSECT",EDGE,{"derivedFrom":[makeQuery(id+"F1.opExtrude","SWEPT_FACE",FACE,{"disambiguationData":[OSD([sQuery(id+"F0.wireOp",EDGE,"E7")])]}),makeQuery(id+"F17.opExtrude","CAP_FACE",FACE,{"disambiguationData":[OSD([sQuery(id+"F16.wireOp",EDGE,"E56.bottom"),sQuery(id+"F16.wireOp",EDGE,"E56.top"),sQuery(id+"F16.wireOp",EDGE,"E56.left"),sQuery(id+"F16.wireOp",EDGE,"E56.right")])],"isStart":true})]});
            var Q18;
            Q18=makeQuery(id+"F17.boolean.opBoolean","INTERSECT",EDGE,{"disambiguationData":[OD(2.0)],"derivedFrom":[makeQuery(id+"F3.boolean.opBoolean","MERGE",FACE,{"derivedFrom":[makeQuery(id+"F1.opExtrude","SWEPT_FACE",FACE,{"disambiguationData":[OSD([sQuery(id+"F0.wireOp",EDGE,"E8")])]}),makeQuery(id+"F1.opExtrude","SWEPT_FACE",FACE,{"disambiguationData":[OSD([sQuery(id+"F0.wireOp",EDGE,"E12.MirrorCS")])]}),makeQuery(id+"F3.opExtrude","SWEPT_FACE",FACE,{"disambiguationData":[OSD([sQuery(id+"F2.wireOp",EDGE,"E31.bottom")])]})]}),makeQuery(id+"F17.opExtrude","CAP_FACE",FACE,{"disambiguationData":[OSD([sQuery(id+"F16.wireOp",EDGE,"E56.bottom"),sQuery(id+"F16.wireOp",EDGE,"E56.top"),sQuery(id+"F16.wireOp",EDGE,"E56.left"),sQuery(id+"F16.wireOp",EDGE,"E56.right")])],"isStart":true})]});
            var Q19;
            Q19=makeQuery(id+"F17.boolean.opBoolean","INTERSECT",EDGE,{"disambiguationData":[OD(0.0)],"derivedFrom":[makeQuery(id+"F1.opExtrude","SWEPT_FACE",FACE,{"disambiguationData":[OSD([sQuery(id+"F0.wireOp",EDGE,"E14")])]}),makeQuery(id+"F17.opExtrude","CAP_FACE",FACE,{"disambiguationData":[OSD([sQuery(id+"F16.wireOp",EDGE,"E56.bottom"),sQuery(id+"F16.wireOp",EDGE,"E56.top"),sQuery(id+"F16.wireOp",EDGE,"E56.left"),sQuery(id+"F16.wireOp",EDGE,"E56.right")])],"isStart":true})]});
            var Q20;
            Q20=makeQuery(id+"F17.boolean.opBoolean","INTERSECT",EDGE,{"disambiguationData":[OD(0.0)],"derivedFrom":[makeQuery(id+"F1.opExtrude","SWEPT_FACE",FACE,{"disambiguationData":[OSD([sQuery(id+"F0.wireOp",EDGE,"E10")])]}),makeQuery(id+"F17.opExtrude","CAP_FACE",FACE,{"disambiguationData":[OSD([sQuery(id+"F16.wireOp",EDGE,"E56.bottom"),sQuery(id+"F16.wireOp",EDGE,"E56.top"),sQuery(id+"F16.wireOp",EDGE,"E56.left"),sQuery(id+"F16.wireOp",EDGE,"E56.right")])],"isStart":true})]});
            var Q21;
            Q21=makeQuery(id+"F17.boolean.opBoolean","INTERSECT",EDGE,{"disambiguationData":[OD(1.0)],"derivedFrom":[makeQuery(id+"F1.opExtrude","SWEPT_FACE",FACE,{"disambiguationData":[OSD([sQuery(id+"F0.wireOp",EDGE,"E10")])]}),makeQuery(id+"F17.opExtrude","CAP_FACE",FACE,{"disambiguationData":[OSD([sQuery(id+"F16.wireOp",EDGE,"E56.bottom"),sQuery(id+"F16.wireOp",EDGE,"E56.top"),sQuery(id+"F16.wireOp",EDGE,"E56.left"),sQuery(id+"F16.wireOp",EDGE,"E56.right")])],"isStart":true})]});
            var Q22;
            Q22=makeQuery(id+"F17.boolean.opBoolean","INTERSECT",EDGE,{"disambiguationData":[OD(1.0)],"derivedFrom":[makeQuery(id+"F1.opExtrude","SWEPT_FACE",FACE,{"disambiguationData":[OSD([sQuery(id+"F0.wireOp",EDGE,"E14")])]}),makeQuery(id+"F17.opExtrude","CAP_FACE",FACE,{"disambiguationData":[OSD([sQuery(id+"F16.wireOp",EDGE,"E56.bottom"),sQuery(id+"F16.wireOp",EDGE,"E56.top"),sQuery(id+"F16.wireOp",EDGE,"E56.left"),sQuery(id+"F16.wireOp",EDGE,"E56.right")])],"isStart":true})]});
            var Q23;
            Q23=makeQuery(id+"F17.boolean.opBoolean","INTERSECT",EDGE,{"disambiguationData":[OD(3.0)],"derivedFrom":[makeQuery(id+"F3.boolean.opBoolean","MERGE",FACE,{"derivedFrom":[makeQuery(id+"F1.opExtrude","SWEPT_FACE",FACE,{"disambiguationData":[OSD([sQuery(id+"F0.wireOp",EDGE,"E8")])]}),makeQuery(id+"F1.opExtrude","SWEPT_FACE",FACE,{"disambiguationData":[OSD([sQuery(id+"F0.wireOp",EDGE,"E12.MirrorCS")])]}),makeQuery(id+"F3.opExtrude","SWEPT_FACE",FACE,{"disambiguationData":[OSD([sQuery(id+"F2.wireOp",EDGE,"E31.bottom")])]})]}),makeQuery(id+"F17.opExtrude","CAP_FACE",FACE,{"disambiguationData":[OSD([sQuery(id+"F16.wireOp",EDGE,"E56.bottom"),sQuery(id+"F16.wireOp",EDGE,"E56.top"),sQuery(id+"F16.wireOp",EDGE,"E56.left"),sQuery(id+"F16.wireOp",EDGE,"E56.right")])],"isStart":true})]});
            var Q24;
            Q24=makeQuery(id+"F9.boolean.opBoolean","INTERSECT",EDGE,{"derivedFrom":[makeQuery(id+"F1.opExtrude","SWEPT_FACE",FACE,{"disambiguationData":[OSD([sQuery(id+"F0.wireOp",EDGE,"E10")])]}),makeQuery(id+"F9.opExtrude","CAP_FACE",FACE,{"disambiguationData":[OSD([sQuery(id+"F8.wireOp",EDGE,"E49")])],"isStart":true})]});
            var Q25;
            Q25=makeQuery(id+"F9.boolean.opBoolean","INTERSECT",EDGE,{"derivedFrom":[makeQuery(id+"F1.opExtrude","SWEPT_FACE",FACE,{"disambiguationData":[OSD([sQuery(id+"F0.wireOp",EDGE,"E14")])]}),makeQuery(id+"F9.opExtrude","CAP_FACE",FACE,{"disambiguationData":[OSD([sQuery(id+"F8.wireOp",EDGE,"E50.MirrorC")])],"isStart":true})]});
            chamfer(context, id + "F24", {"entities" : qUnion([Q0, Q1, Q2, Q3, Q4, Q5, Q6, Q7, Q8, Q9, Q10, Q11, Q12, Q13, Q14, Q15, Q16, Q17, Q18, Q19, Q20, Q21, Q22, Q23, Q24, Q25]), "width" : 0.75 * mm, "tangentPropagation" : true});
        }
    });
